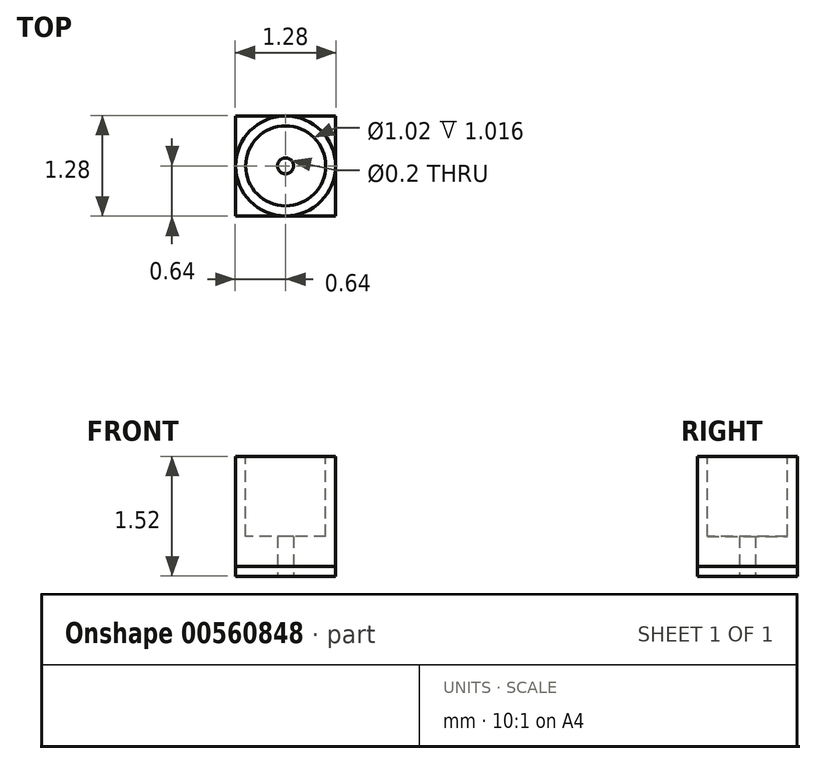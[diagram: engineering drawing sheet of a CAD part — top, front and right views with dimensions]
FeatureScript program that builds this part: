
annotation { "Feature Type Name" : "Feature", "Feature Type Description" : "" }
export const myFeature = defineFeature(function(context is Context, id is Id, definition is map)
    precondition{}
    {
        {
            var Q0;
            Q0=qCreatedBy(makeId("Top.planeOp"),FACE);
            var sketch = newSketch(context, id + "F0", { "sketchPlane" : qUnion([Q0])});
            skCircle(sketch, "E0", {"center": v(0, 0) * mm, "radius": 0.64 * mm});
            skSolve(sketch);
        }
        {
            var Q0;
            Q0=makeQuery(id+"F0.imprint","IMPRINT",FACE,{"disambiguationData":[TD([[makeQuery(id+"F0.imprint","IMPRINT",EDGE,{"derivedFrom":sQuery(id+"F0.wireOp",EDGE,"E0")}),1.0]])]});
            extrude(context, id + "F1", {"entities" : qUnion([Q0]), "depth" : 1.27 * mm, "offsetDistance" : 25.4 * mm});
        }
        {
            var Q0;
            Q0=makeQuery(id+"F1.opExtrude","CAP_FACE",FACE,{"disambiguationData":[OSD([sQuery(id+"F0.wireOp",EDGE,"E0")])],"isStart":false});
            var sketch = newSketch(context, id + "F2", { "sketchPlane" : qUnion([Q0])});
            skCircle(sketch, "E1", {"center": v(0, 0) * mm, "radius": 0.5 * mm});
            skSolve(sketch);
        }
        {
            var Q0;
            Q0=makeQuery(id+"F2.imprint","IMPRINT",FACE,{"disambiguationData":[TD([[makeQuery(id+"F2.imprint","IMPRINT",EDGE,{"derivedFrom":sQuery(id+"F2.wireOp",EDGE,"E1")}),1.0]])]});
            extrude(context, id + "F3", {"entities" : qUnion([Q0]), "operationType" : NewBodyOperationType.REMOVE, "oppositeDirection" : true, "depth" : 1.02 * mm, "offsetDistance" : 25.4 * mm});
        }
        {
            var Q0;
            Q0=makeQuery(id+"F1.opExtrude","CAP_FACE",FACE,{"disambiguationData":[OSD([sQuery(id+"F0.wireOp",EDGE,"E0")])],"isStart":true});
            var sketch = newSketch(context, id + "F4", { "sketchPlane" : qUnion([Q0])});
            skLineSegment(sketch, "E2.bottom", {"start": v(0.64, 0.64) * mm, "end": v(-0.64, 0.64) * mm});
            skLineSegment(sketch, "E2.top", {"start": v(0.64, -0.64) * mm, "end": v(-0.64, -0.64) * mm});
            skLineSegment(sketch, "E2.left", {"start": v(0.64, 0.64) * mm, "end": v(0.64, -0.64) * mm});
            skLineSegment(sketch, "E2.right", {"start": v(-0.64, 0.64) * mm, "end": v(-0.64, -0.64) * mm});
            skPoint(sketch, "E2.middle", {"position": v(0, 0) * mm});
            skSolve(sketch);
        }
        {
            var Q0;
            {var subQ0=sQuery(id+"F4.wireOp",EDGE,"E2.right");var subQ1=sQuery(id+"F4.wireOp",EDGE,"E2.top");var subQ2=makeQuery(id+"F4.imprint","INTERSECT",VERTEX,{"derivedFrom":[subQ1,subQ0]});Q0=makeQuery(id+"F4.imprint","IMPRINT",FACE,{"disambiguationData":[TD([[makeQuery(id+"F4.imprint","IMPRINT",EDGE,{"disambiguationData":[TD([[subQ2,1.0]])],"derivedFrom":subQ1}),-1.0]])]});}
            var Q1;
            {var subQ0=sQuery(id+"F4.wireOp",EDGE,"E2.left");var subQ1=sQuery(id+"F4.wireOp",EDGE,"E2.top");var subQ2=makeQuery(id+"F4.imprint","INTERSECT",VERTEX,{"derivedFrom":[subQ1,subQ0]});Q1=makeQuery(id+"F4.imprint","IMPRINT",FACE,{"disambiguationData":[TD([[makeQuery(id+"F4.imprint","IMPRINT",EDGE,{"disambiguationData":[TD([[subQ2,-1.0]])],"derivedFrom":subQ1}),-1.0]])]});}
            var Q2;
            {var subQ0=sQuery(id+"F4.wireOp",EDGE,"E2.left");var subQ1=sQuery(id+"F4.wireOp",EDGE,"E2.bottom");var subQ2=makeQuery(id+"F4.imprint","INTERSECT",VERTEX,{"derivedFrom":[subQ1,subQ0]});Q2=makeQuery(id+"F4.imprint","IMPRINT",FACE,{"disambiguationData":[TD([[makeQuery(id+"F4.imprint","IMPRINT",EDGE,{"disambiguationData":[TD([[subQ2,-1.0]])],"derivedFrom":subQ1}),1.0]])]});}
            var Q3;
            {var subQ0=sQuery(id+"F4.wireOp",EDGE,"E2.right");var subQ1=sQuery(id+"F4.wireOp",EDGE,"E2.bottom");var subQ2=makeQuery(id+"F4.imprint","INTERSECT",VERTEX,{"derivedFrom":[subQ1,subQ0]});Q3=makeQuery(id+"F4.imprint","IMPRINT",FACE,{"disambiguationData":[TD([[makeQuery(id+"F4.imprint","IMPRINT",EDGE,{"disambiguationData":[TD([[subQ2,1.0]])],"derivedFrom":subQ1}),1.0]])]});}
            var Q4;
            {var subQ0=makeQuery(id+"F1.opExtrude","CAP_EDGE",EDGE,{"disambiguationData":[OSD([sQuery(id+"F0.wireOp",EDGE,"E0")])],"isStart":true});var subQ1=makeQuery(id+"F4.imprint","INTERSECT",VERTEX,{"derivedFrom":[subQ0,sQuery(id+"F4.wireOp",EDGE,"E2.bottom")]});Q4=makeQuery(id+"F4.imprint","IMPRINT",FACE,{"disambiguationData":[TD([[makeQuery(id+"F4.imprint","IMPRINT",EDGE,{"disambiguationData":[TD([[subQ1,-1.0]])],"derivedFrom":subQ0}),-1.0]])]});}
            extrude(context, id + "F5", {"entities" : qUnion([Q0, Q1, Q2, Q3, Q4]), "operationType" : NewBodyOperationType.ADD, "depth" : 0.25 * mm, "offsetDistance" : 25.4 * mm});
        }
        {
            var Q0;
            {var subQ0=sQuery(id+"F4.wireOp",EDGE,"E2.top");var subQ1=sQuery(id+"F4.wireOp",EDGE,"E2.right");var subQ2=makeQuery(id+"F5.opExtrude","CAP_FACE",FACE,{"disambiguationData":[OSD([sQuery(id+"F4.wireOp",EDGE,"E2.bottom"),subQ0,sQuery(id+"F4.wireOp",EDGE,"E2.left"),subQ1])],"isStart":true});Q0=makeQuery(id+"F5.boolean.opBoolean","SPLIT",FACE,{"disambiguationData":[TD([makeQuery(id+"F1.opExtrude","SWEPT_FACE",FACE,{"disambiguationData":[OSD([sQuery(id+"F0.wireOp",EDGE,"E0")])]}),subQ2,makeQuery(id+"F5.opExtrude","SWEPT_FACE",FACE,{"disambiguationData":[OSD([subQ0])]}),makeQuery(id+"F5.opExtrude","SWEPT_FACE",FACE,{"disambiguationData":[OSD([subQ1])]})])],"derivedFrom":subQ2});}
            var Q1;
            {var subQ0=sQuery(id+"F4.wireOp",EDGE,"E2.bottom");var subQ1=sQuery(id+"F4.wireOp",EDGE,"E2.right");var subQ2=makeQuery(id+"F5.opExtrude","CAP_FACE",FACE,{"disambiguationData":[OSD([subQ0,sQuery(id+"F4.wireOp",EDGE,"E2.top"),sQuery(id+"F4.wireOp",EDGE,"E2.left"),subQ1])],"isStart":true});Q1=makeQuery(id+"F5.boolean.opBoolean","SPLIT",FACE,{"disambiguationData":[TD([makeQuery(id+"F1.opExtrude","SWEPT_FACE",FACE,{"disambiguationData":[OSD([sQuery(id+"F0.wireOp",EDGE,"E0")])]}),makeQuery(id+"F5.opExtrude","SWEPT_FACE",FACE,{"disambiguationData":[OSD([subQ0])]}),subQ2,makeQuery(id+"F5.opExtrude","SWEPT_FACE",FACE,{"disambiguationData":[OSD([subQ1])]})])],"derivedFrom":subQ2});}
            var Q2;
            {var subQ0=sQuery(id+"F4.wireOp",EDGE,"E2.bottom");var subQ1=sQuery(id+"F4.wireOp",EDGE,"E2.left");var subQ2=makeQuery(id+"F5.opExtrude","CAP_FACE",FACE,{"disambiguationData":[OSD([subQ0,sQuery(id+"F4.wireOp",EDGE,"E2.top"),subQ1,sQuery(id+"F4.wireOp",EDGE,"E2.right")])],"isStart":true});Q2=makeQuery(id+"F5.boolean.opBoolean","SPLIT",FACE,{"disambiguationData":[TD([makeQuery(id+"F1.opExtrude","SWEPT_FACE",FACE,{"disambiguationData":[OSD([sQuery(id+"F0.wireOp",EDGE,"E0")])]}),makeQuery(id+"F5.opExtrude","SWEPT_FACE",FACE,{"disambiguationData":[OSD([subQ0])]}),subQ2,makeQuery(id+"F5.opExtrude","SWEPT_FACE",FACE,{"disambiguationData":[OSD([subQ1])]})])],"derivedFrom":subQ2});}
            var Q3;
            {var subQ0=sQuery(id+"F4.wireOp",EDGE,"E2.top");var subQ1=sQuery(id+"F4.wireOp",EDGE,"E2.left");var subQ2=makeQuery(id+"F5.opExtrude","CAP_FACE",FACE,{"disambiguationData":[OSD([sQuery(id+"F4.wireOp",EDGE,"E2.bottom"),subQ0,subQ1,sQuery(id+"F4.wireOp",EDGE,"E2.right")])],"isStart":true});Q3=makeQuery(id+"F5.boolean.opBoolean","SPLIT",FACE,{"disambiguationData":[TD([makeQuery(id+"F1.opExtrude","SWEPT_FACE",FACE,{"disambiguationData":[OSD([sQuery(id+"F0.wireOp",EDGE,"E0")])]}),subQ2,makeQuery(id+"F5.opExtrude","SWEPT_FACE",FACE,{"disambiguationData":[OSD([subQ0])]}),makeQuery(id+"F5.opExtrude","SWEPT_FACE",FACE,{"disambiguationData":[OSD([subQ1])]})])],"derivedFrom":subQ2});}
            extrude(context, id + "F6", {"entities" : qUnion([Q0, Q1, Q2, Q3]), "operationType" : NewBodyOperationType.REMOVE, "oppositeDirection" : true, "depth" : 0.13 * mm, "offsetDistance" : 25.4 * mm});
        }
        {
            var Q0;
            Q0=makeQuery(id+"F5.opExtrude","CAP_FACE",FACE,{"disambiguationData":[OSD([sQuery(id+"F4.wireOp",EDGE,"E2.bottom"),sQuery(id+"F4.wireOp",EDGE,"E2.top"),sQuery(id+"F4.wireOp",EDGE,"E2.left"),sQuery(id+"F4.wireOp",EDGE,"E2.right")])],"isStart":false});
            var sketch = newSketch(context, id + "F7", { "sketchPlane" : qUnion([Q0])});
            skCircle(sketch, "E3", {"center": v(0, 0) * mm, "radius": 0.1 * mm});
            skSolve(sketch);
        }
        {
            var Q0;
            Q0 = qSketchRegion(id + "F7", true);
            extrude(context, id + "F8", {"entities" : qUnion([Q0]), "operationType" : NewBodyOperationType.REMOVE, "oppositeDirection" : true, "depth" : 25.4 * mm, "offsetDistance" : 25.4 * mm});
        }
    });
